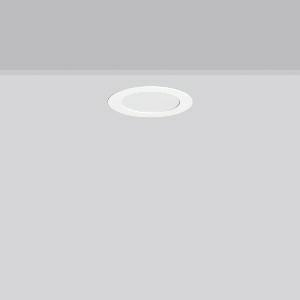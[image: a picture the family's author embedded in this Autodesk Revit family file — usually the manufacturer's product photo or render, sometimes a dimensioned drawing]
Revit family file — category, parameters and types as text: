
# Revit family: toledo_flat__round_e_901807_002_2_730_2ac4
name_source: partatom
category: Lighting Fixtures
units: mm (PartAtom-declared; Revit-internal decimal feet)

## family parameters
Cut with Voids When Loaded = No
Host = Face
Light Source = No
Part Type = Normal
Room Calculation Point = No
Round Connector Dimension = Use Diameter
Shared = No

## types (1)
- TuneableWhite 827 (1 x LED Modul 827, 860 lm, 2700)
    Apparent Load = 10 VA
    CIE Flux Codes = 47 79 96 100 100
    Color Rendering = 80
    Color Temperature = 2700
    Default Elevation = 1800 mm
    Description = Series: TOLEDO FLAT+ round
Flexible round recessed multifunction downlight. Housing: sheet steel, powder-coated. Luminaire frame: aluminium, powder-coated. Light guide and diffuser made of non-yellowing PMMA, opal matt. LED backlight technology for homogeneous illumination of the entire light-emitting surface. Tunable white dynamically adjustable from 2700 K to 6500 K. Suitable for Recessed ceiling mounting. Ceiling installation with spring system. Can be directly covered with thermal insulation material (applies only to the lower lumen levels). Including separate LED converter with connecting cable 250 mm. With Casambi smart+free Bluetooth control for wireless network and operation using Android / iOS devices, free app available for download. Surface mounted housing as accessory for all sizes. 
Colour: white
Diameter: 165 mm
Height: 2 mm
Cut-out diameter: 152 mm
Recess height: 90 mm
Luminaire: recess height: 35 mm
Lamp: LED
Socket: without socket
Colour temperature: 2700K - 6500K
Colour rendering index (CRI): 80
System power: 10 W
Rated luminous flux: 860 lm
Luminous efficiency: 86 lm/W
System power 2: 10 W
Rated luminous flux 2: 890 lm
Luminous efficiency 2: 89 lm/W
System power 3: 10 W
Rated luminous flux 3: 890 lm
Luminous efficiency 3: 89 lm/W
Control gear: Dimmable Bluetooth converter
Protection class: II
Type of protection: IP 54
    Height = 0 mm  [stored 0 ft]
    Lamp = 1 x LED Modul 827
    Lamp Light Flux = 860 lm
    Lamp count = 1
    Length = 165 mm
    Lifetime = 50000 h
    Luminous efficacy = 86 lm/W
    Manufacturer = RZB
    ModVariant = No
    Model = 901807.002.2.730
    Mounting Place = Ceiling
    Mounting Type = Recessed
    Number of Poles = 1
    OnlyDefault = Yes
    Power Factor = 1
    Product Name = TOLEDO FLAT+ round E
    Product group = Recessed downlights
    ProductGroupID = 402
    Protection Class = Protection class II
    Protection Degree = Degree of protection
    RLX_Detail_Level = 1
    RLX_Emergency_Light_Flux = 0 lm
    RLX_Emergency_Type = 0
    RLX_Emergency_Type_DB = No
    RlxData = <blob elided: 27541 chars, md5=2095143e>
    Socket = socket
    Standby Power = 0 W
    System Light Flux = 860 lm
    System Power = 10 W
    Type Comments = TuneableWhite 827
    Type Image = 901807.002.jpg
    URL = http://relux.com
    VarID = tuneablewhite_827
    Voltage = 0 V
    Weight = 0.00 kg
    Width = 0 mm  [stored 0 ft]

note: [stored X ft] marks values corroborated as IEEE doubles in the binary element streams (Revit-internal decimal feet)

## geometry (parser evidence)
native form markers: Blend x4, Sweep x11
no freeform markers — native parametric forms only
